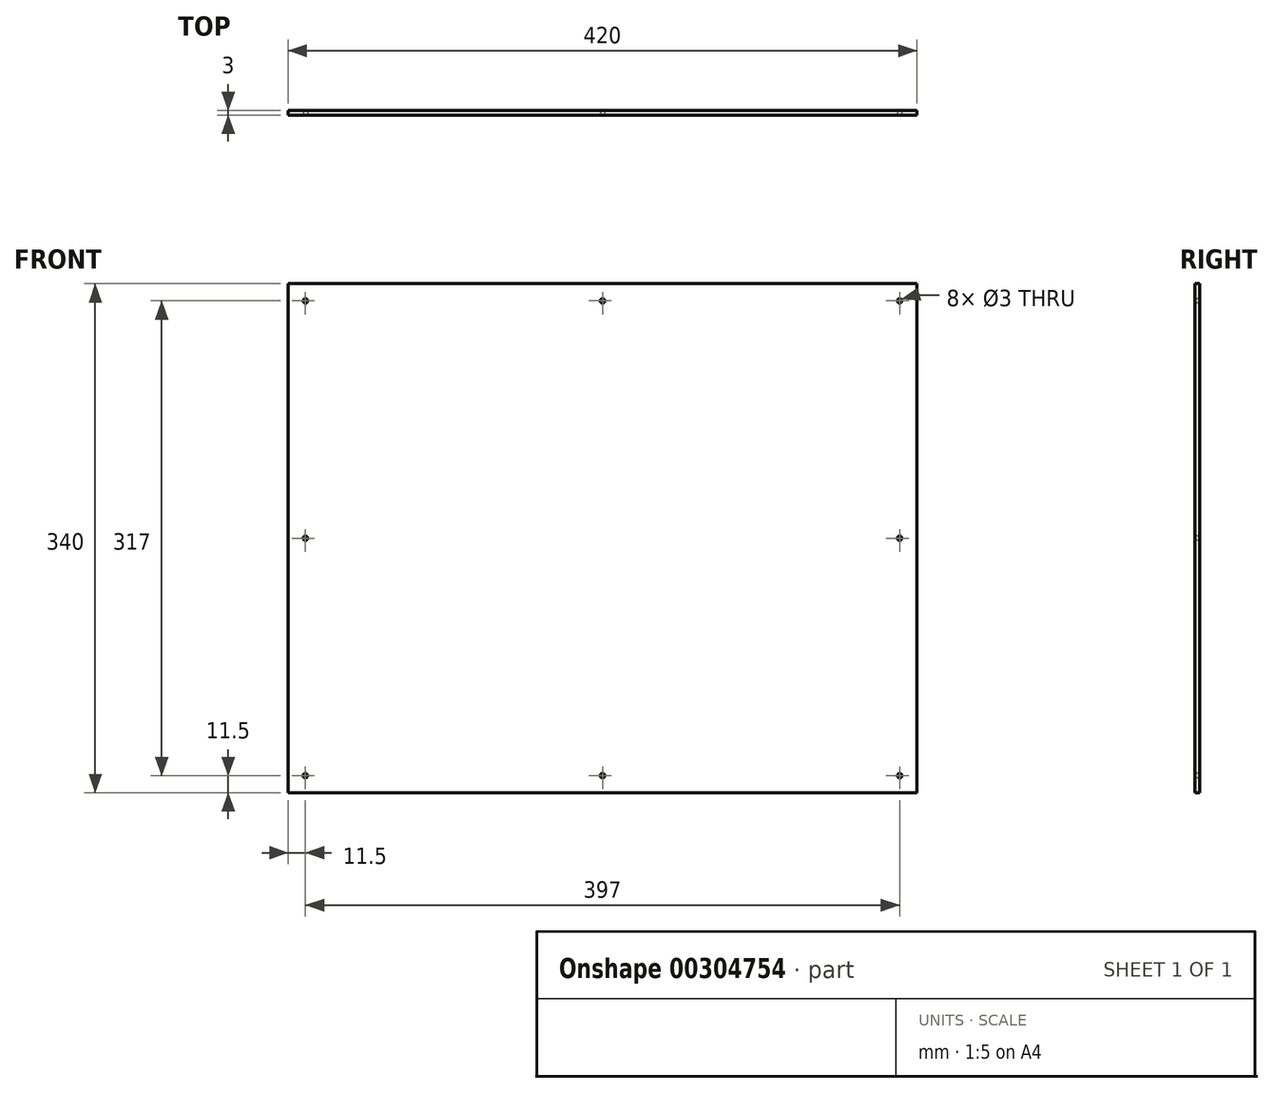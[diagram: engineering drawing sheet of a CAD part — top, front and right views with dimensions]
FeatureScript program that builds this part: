
annotation { "Feature Type Name" : "Feature", "Feature Type Description" : "" }
export const myFeature = defineFeature(function(context is Context, id is Id, definition is map)
    precondition{}
    {
        {
            var Q0;
            Q0=qCreatedBy(makeId("Front.planeOp"),FACE);
            var sketch = newSketch(context, id + "F0", { "sketchPlane" : qUnion([Q0])});
            skLineSegment(sketch, "E0.bottom", {"start": v(210, -170) * mm, "end": v(-210, -170) * mm});
            skLineSegment(sketch, "E0.top", {"start": v(210, 170) * mm, "end": v(-210, 170) * mm});
            skLineSegment(sketch, "E0.left", {"start": v(210, -170) * mm, "end": v(210, 170) * mm});
            skLineSegment(sketch, "E0.right", {"start": v(-210, -170) * mm, "end": v(-210, 170) * mm});
            skPoint(sketch, "E0.middle", {"position": v(0, 0) * mm});
            skSolve(sketch);
        }
        {
            var Q0;
            Q0=makeQuery(id+"F0.imprint","IMPRINT",FACE,{"disambiguationData":[TD([[makeQuery(id+"F0.imprint","IMPRINT",EDGE,{"derivedFrom":sQuery(id+"F0.wireOp",EDGE,"E0.bottom")}),-1.0]])]});
            extrude(context, id + "F1", {"entities" : qUnion([Q0]), "endBound" : BoundingType.SYMMETRIC, "depth" : 3 * mm});
        }
        {
            var Q0;
            Q0=makeQuery(id+"F1.opExtrude","CAP_FACE",FACE,{"disambiguationData":[OSD([sQuery(id+"F0.wireOp",EDGE,"E0.bottom"),sQuery(id+"F0.wireOp",EDGE,"E0.top"),sQuery(id+"F0.wireOp",EDGE,"E0.left"),sQuery(id+"F0.wireOp",EDGE,"E0.right")])],"isStart":false});
            var sketch = newSketch(context, id + "F2", { "sketchPlane" : qUnion([Q0])});
            skCircle(sketch, "E1", {"center": v(-198.5, 158.5) * mm, "radius": 1.5 * mm});
            skCircle(sketch, "E2", {"center": v(198.5, -158.5) * mm, "radius": 1.5 * mm});
            skCircle(sketch, "E3", {"center": v(198.5, 158.5) * mm, "radius": 1.5 * mm});
            skCircle(sketch, "E4", {"center": v(0, 158.5) * mm, "radius": 1.5 * mm});
            skCircle(sketch, "E5", {"center": v(198.5, 0) * mm, "radius": 1.5 * mm});
            skCircle(sketch, "E6", {"center": v(-198.5, -158.5) * mm, "radius": 1.5 * mm});
            skCircle(sketch, "E7", {"center": v(-198.5, 0) * mm, "radius": 1.5 * mm});
            skCircle(sketch, "E8", {"center": v(0, -158.5) * mm, "radius": 1.5 * mm});
            skSolve(sketch);
        }
        {
            var Q0;
            Q0 = qSketchRegion(id + "F2", true);
            extrude(context, id + "F3", {"entities" : qUnion([Q0]), "operationType" : NewBodyOperationType.REMOVE, "oppositeDirection" : true, "depth" : 25 * mm});
        }
    });
